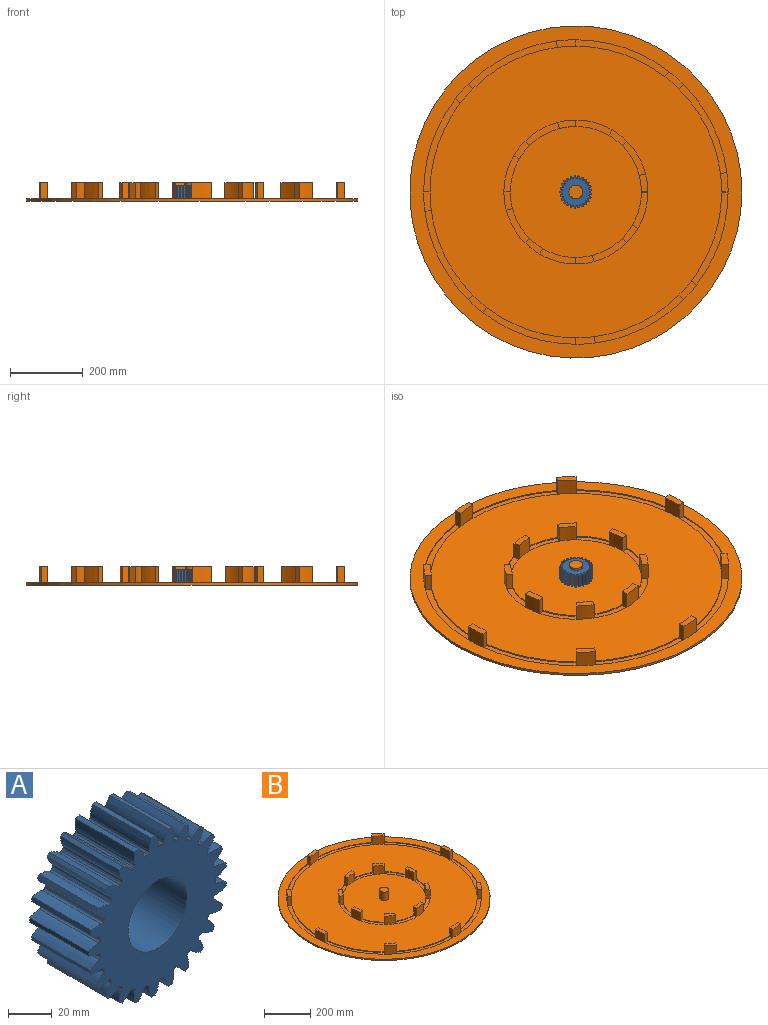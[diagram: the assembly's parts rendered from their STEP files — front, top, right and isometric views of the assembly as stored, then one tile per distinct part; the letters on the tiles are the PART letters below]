
ASSEMBLY  parts=2 mates=1
PART A: 153 faces, bbox 88.9x38.1x89.1 mm
  f0: cylinder r=44.58mm len=38.1mm, axis (0,1,0), area 90.4mm2, adj f24,f26,f137,f149
  f1: cylinder r=44.58mm len=38.1mm, axis (0,1,0), area 90.4mm2, adj f24,f26,f144,f147
  f2: cylinder r=44.58mm len=38.1mm, axis (0,1,0), area 90.4mm2, adj f24,f26,f132,f139
  f3: cylinder r=44.58mm len=38.1mm, axis (0,1,0), area 90.4mm2, adj f24,f26,f127,f134
  f4: cylinder r=44.58mm len=38.1mm, axis (0,1,0), area 90.4mm2, adj f24,f26,f122,f129
  f5: cylinder r=44.58mm len=38.1mm, axis (0,1,0), area 90.4mm2, adj f24,f26,f112,f124
  f6: cylinder r=44.58mm len=38.1mm, axis (0,1,0), area 90.4mm2, adj f24,f26,f107,f119
  f7: cylinder r=44.58mm len=38.1mm, axis (0,1,0), area 90.4mm2, adj f24,f26,f114,f117
  f8: cylinder r=44.58mm len=38.1mm, axis (0,1,0), area 90.4mm2, adj f24,f26,f102,f109
  f9: cylinder r=44.58mm len=38.1mm, axis (0,1,0), area 90.4mm2, adj f24,f26,f97,f104
  f10: cylinder r=44.58mm len=38.1mm, axis (0,1,0), area 90.4mm2, adj f24,f26,f92,f99
  f11: cylinder r=44.58mm len=38.1mm, axis (0,1,0), area 90.4mm2, adj f24,f26,f77,f94
  f12: cylinder r=44.58mm len=38.1mm, axis (0,1,0), area 90.4mm2, adj f24,f26,f27,f89
  f13: cylinder r=44.58mm len=38.1mm, axis (0,1,0), area 90.4mm2, adj f24,f26,f84,f87
  f14: cylinder r=44.58mm len=38.1mm, axis (0,1,0), area 90.4mm2, adj f24,f26,f72,f79
  f15: cylinder r=44.58mm len=38.1mm, axis (0,1,0), area 90.4mm2, adj f24,f26,f74,f82
  f16: cylinder r=44.58mm len=38.1mm, axis (0,1,0), area 90.4mm2, adj f24,f26,f69,f142
  f17: cylinder r=44.58mm len=38.1mm, axis (0,1,0), area 90.4mm2, adj f24,f26,f64,f67
  f18: cylinder r=44.58mm len=38.1mm, axis (0,1,0), area 90.4mm2, adj f24,f26,f59,f62
  f19: cylinder r=44.58mm len=38.1mm, axis (0,1,0), area 90.4mm2, adj f24,f26,f54,f57
  f20: cylinder r=44.58mm len=38.1mm, axis (0,1,0), area 90.4mm2, adj f24,f26,f42,f49
  f21: cylinder r=44.58mm len=38.1mm, axis (0,1,0), area 90.4mm2, adj f24,f26,f32,f44
  f22: cylinder r=44.58mm len=38.1mm, axis (0,1,0), area 90.4mm2, adj f24,f26,f39,f52
  f23: cylinder r=44.58mm len=38.1mm, axis (0,1,0), area 90.4mm2, adj f24,f26,f34,f37
  f24: plane 89.11x88.94mm, normal (0,-1,0), area 4133mm2, adj f0,f1,f2,f3,f4,f5,f6,f7
  f25: cylinder r=44.58mm len=38.1mm, axis (0,1,0), area 90.4mm2, adj f24,f26,f29,f47
  f26: plane 89.11x88.94mm, normal (0,1,0), area 4133mm2, adj f0,f1,f2,f3,f4,f5,f6,f7
  f27: extruded ~38.1x6.03mm, area 252.8mm2, adj f12,f24,f26,f30
  f28: cylinder r=37.15mm len=38.1mm, axis (0,1,0), area 43.2mm2, adj f24,f26,f30,f31
  f29: extruded ~38.1x6.03mm, area 252.8mm2, adj f24,f25,f26,f31
  f30: cylinder r=1.25mm len=38.1mm, axis (0,1,0), area 73.2mm2, adj f24,f26,f27,f28
  f31: cylinder r=1.25mm len=38.1mm, axis (0,1,0), area 73.2mm2, adj f24,f26,f28,f29
  f32: extruded ~38.1x6.16mm, area 252.8mm2, adj f21,f24,f26,f35
  f33: cylinder r=37.15mm len=38.1mm, axis (0,1,0), area 43.2mm2, adj f24,f26,f35,f36
  f34: extruded ~38.1x6mm, area 252.8mm2, adj f23,f24,f26,f36
  f35: cylinder r=1.25mm len=38.1mm, axis (0,1,0), area 73.2mm2, adj f24,f26,f32,f33
  f36: cylinder r=1.25mm len=38.1mm, axis (0,1,0), area 73.2mm2, adj f24,f26,f33,f34
  f37: extruded ~38.1x5.4mm, area 252.8mm2, adj f23,f24,f26,f40
  f38: cylinder r=37.15mm len=38.1mm, axis (0,1,0), area 43.2mm2, adj f24,f26,f40,f41
  f39: extruded ~38.1x6.47mm, area 252.8mm2, adj f22,f24,f26,f41
  f40: cylinder r=1.25mm len=38.1mm, axis (0,1,0), area 73.2mm2, adj f24,f26,f37,f38
  f41: cylinder r=1.25mm len=38.1mm, axis (0,1,0), area 73.2mm2, adj f24,f26,f38,f39
  f42: extruded ~38.1x6.52mm, area 252.8mm2, adj f20,f24,f26,f45
  f43: cylinder r=37.15mm len=38.1mm, axis (0,1,0), area 43.2mm2, adj f24,f26,f45,f46
  f44: extruded ~38.1x5.16mm, area 252.8mm2, adj f21,f24,f26,f46
  f45: cylinder r=1.25mm len=38.1mm, axis (0,1,0), area 73.2mm2, adj f24,f26,f42,f43
  f46: cylinder r=1.25mm len=38.1mm, axis (0,1,0), area 73.2mm2, adj f24,f26,f43,f44
  f47: extruded ~38.1x6.48mm, area 252.8mm2, adj f24,f25,f26,f50
  f48: cylinder r=37.15mm len=38.1mm, axis (0,1,0), area 43.2mm2, adj f24,f26,f50,f51
  f49: extruded ~38.1x5.2mm, area 252.8mm2, adj f20,f24,f26,f51
  f50: cylinder r=1.25mm len=38.1mm, axis (0,1,0), area 73.2mm2, adj f24,f26,f47,f48
  f51: cylinder r=1.25mm len=38.1mm, axis (0,1,0), area 73.2mm2, adj f24,f26,f48,f49
  f52: extruded ~38.1x4.94mm, area 252.8mm2, adj f22,f24,f26,f55
  f53: cylinder r=37.15mm len=38.1mm, axis (0,1,0), area 43.2mm2, adj f24,f26,f55,f56
  f54: extruded ~38.1x6.53mm, area 252.8mm2, adj f19,f24,f26,f56
  f55: cylinder r=1.25mm len=38.1mm, axis (0,1,0), area 73.2mm2, adj f24,f26,f52,f53
  f56: cylinder r=1.25mm len=38.1mm, axis (0,1,0), area 73.2mm2, adj f24,f26,f53,f54
  f57: extruded ~38.1x5.85mm, area 252.8mm2, adj f19,f24,f26,f60
  f58: cylinder r=37.15mm len=38.1mm, axis (0,1,0), area 43.2mm2, adj f24,f26,f60,f61
  f59: extruded ~38.1x6.18mm, area 252.8mm2, adj f18,f24,f26,f61
  f60: cylinder r=1.25mm len=38.1mm, axis (0,1,0), area 73.2mm2, adj f24,f26,f57,f58
  f61: cylinder r=1.25mm len=38.1mm, axis (0,1,0), area 73.2mm2, adj f24,f26,f58,f59
  f62: extruded ~38.1x6.4mm, area 252.8mm2, adj f18,f24,f26,f65
  f63: cylinder r=37.15mm len=38.1mm, axis (0,1,0), area 43.2mm2, adj f24,f26,f65,f66
  f64: extruded ~38.1x5.44mm, area 252.8mm2, adj f17,f24,f26,f66
  f65: cylinder r=1.25mm len=38.1mm, axis (0,1,0), area 73.2mm2, adj f24,f26,f62,f63
  f66: cylinder r=1.25mm len=38.1mm, axis (0,1,0), area 73.2mm2, adj f24,f26,f63,f64
  f67: extruded ~38.1x6.55mm, area 252.8mm2, adj f17,f24,f26,f70
  f68: cylinder r=37.15mm len=38.1mm, axis (0,1,0), area 43.2mm2, adj f24,f26,f70,f71
  f69: extruded ~38.1x4.89mm, area 252.8mm2, adj f16,f24,f26,f71
  f70: cylinder r=1.25mm len=38.1mm, axis (0,1,0), area 73.2mm2, adj f24,f26,f67,f68
  f71: cylinder r=1.25mm len=38.1mm, axis (0,1,0), area 73.2mm2, adj f24,f26,f68,f69
  f72: extruded ~38.1x6mm, area 252.8mm2, adj f14,f24,f26,f75
  f73: cylinder r=37.15mm len=38.1mm, axis (0,1,0), area 43.2mm2, adj f24,f26,f75,f76
  f74: extruded ~38.1x6.16mm, area 252.8mm2, adj f15,f24,f26,f76
  f75: cylinder r=1.25mm len=38.1mm, axis (0,1,0), area 73.2mm2, adj f24,f26,f72,f73
  f76: cylinder r=1.25mm len=38.1mm, axis (0,1,0), area 73.2mm2, adj f24,f26,f73,f74
  f77: extruded ~38.1x6.47mm, area 252.8mm2, adj f11,f24,f26,f80
  f78: cylinder r=37.15mm len=38.1mm, axis (0,1,0), area 43.2mm2, adj f24,f26,f80,f81
  f79: extruded ~38.1x5.4mm, area 252.8mm2, adj f14,f24,f26,f81
  f80: cylinder r=1.25mm len=38.1mm, axis (0,1,0), area 73.2mm2, adj f24,f26,f77,f78
  f81: cylinder r=1.25mm len=38.1mm, axis (0,1,0), area 73.2mm2, adj f24,f26,f78,f79
  f82: extruded ~38.1x5.16mm, area 252.8mm2, adj f15,f24,f26,f85
  f83: cylinder r=37.15mm len=38.1mm, axis (0,1,0), area 43.2mm2, adj f24,f26,f85,f86
  f84: extruded ~38.1x6.52mm, area 252.8mm2, adj f13,f24,f26,f86
  f85: cylinder r=1.25mm len=38.1mm, axis (0,1,0), area 73.2mm2, adj f24,f26,f82,f83
  f86: cylinder r=1.25mm len=38.1mm, axis (0,1,0), area 73.2mm2, adj f24,f26,f83,f84
  f87: extruded ~38.1x5.2mm, area 252.8mm2, adj f13,f24,f26,f90
  f88: cylinder r=37.15mm len=38.1mm, axis (0,1,0), area 43.2mm2, adj f24,f26,f90,f91
  f89: extruded ~38.1x6.48mm, area 252.8mm2, adj f12,f24,f26,f91
  f90: cylinder r=1.25mm len=38.1mm, axis (0,1,0), area 73.2mm2, adj f24,f26,f87,f88
  f91: cylinder r=1.25mm len=38.1mm, axis (0,1,0), area 73.2mm2, adj f24,f26,f88,f89
  f92: extruded ~38.1x6.53mm, area 252.8mm2, adj f10,f24,f26,f95
  f93: cylinder r=37.15mm len=38.1mm, axis (0,1,0), area 43.2mm2, adj f24,f26,f95,f96
  f94: extruded ~38.1x4.94mm, area 252.8mm2, adj f11,f24,f26,f96
  f95: cylinder r=1.25mm len=38.1mm, axis (0,1,0), area 73.2mm2, adj f24,f26,f92,f93
  f96: cylinder r=1.25mm len=38.1mm, axis (0,1,0), area 73.2mm2, adj f24,f26,f93,f94
  f97: extruded ~38.1x6.18mm, area 252.8mm2, adj f9,f24,f26,f100
  f98: cylinder r=37.15mm len=38.1mm, axis (0,1,0), area 43.2mm2, adj f24,f26,f100,f101
  f99: extruded ~38.1x5.85mm, area 252.8mm2, adj f10,f24,f26,f101
  f100: cylinder r=1.25mm len=38.1mm, axis (0,1,0), area 73.2mm2, adj f24,f26,f97,f98
  f101: cylinder r=1.25mm len=38.1mm, axis (0,1,0), area 73.2mm2, adj f24,f26,f98,f99
  f102: extruded ~38.1x5.44mm, area 252.8mm2, adj f8,f24,f26,f105
  f103: cylinder r=37.15mm len=38.1mm, axis (0,1,0), area 43.2mm2, adj f24,f26,f105,f106
  f104: extruded ~38.1x6.4mm, area 252.8mm2, adj f9,f24,f26,f106
  f105: cylinder r=1.25mm len=38.1mm, axis (0,1,0), area 73.2mm2, adj f24,f26,f102,f103
  f106: cylinder r=1.25mm len=38.1mm, axis (0,1,0), area 73.2mm2, adj f24,f26,f103,f104
  f107: extruded ~38.1x4.89mm, area 252.8mm2, adj f6,f24,f26,f110
  f108: cylinder r=37.15mm len=38.1mm, axis (0,1,0), area 43.2mm2, adj f24,f26,f110,f111
  f109: extruded ~38.1x6.55mm, area 252.8mm2, adj f8,f24,f26,f111
  f110: cylinder r=1.25mm len=38.1mm, axis (0,1,0), area 73.2mm2, adj f24,f26,f107,f108
  f111: cylinder r=1.25mm len=38.1mm, axis (0,1,0), area 73.2mm2, adj f24,f26,f108,f109
  f112: extruded ~38.1x6.39mm, area 252.8mm2, adj f5,f24,f26,f115
  f113: cylinder r=37.15mm len=38.1mm, axis (0,1,0), area 43.2mm2, adj f24,f26,f115,f116
  f114: extruded ~38.1x5.62mm, area 252.8mm2, adj f7,f24,f26,f116
  f115: cylinder r=1.25mm len=38.1mm, axis (0,1,0), area 73.2mm2, adj f24,f26,f112,f113
  f116: cylinder r=1.25mm len=38.1mm, axis (0,1,0), area 73.2mm2, adj f24,f26,f113,f114
  f117: extruded ~38.1x5.82mm, area 252.8mm2, adj f7,f24,f26,f120
  f118: cylinder r=37.15mm len=38.1mm, axis (0,1,0), area 43.2mm2, adj f24,f26,f120,f121
  f119: extruded ~38.1x6.28mm, area 252.8mm2, adj f6,f24,f26,f121
  f120: cylinder r=1.25mm len=38.1mm, axis (0,1,0), area 73.2mm2, adj f24,f26,f117,f118
  f121: cylinder r=1.25mm len=38.1mm, axis (0,1,0), area 73.2mm2, adj f24,f26,f118,f119
  f122: extruded ~38.1x6.55mm, area 252.8mm2, adj f4,f24,f26,f125
  f123: cylinder r=37.15mm len=38.1mm, axis (0,1,0), area 43.2mm2, adj f24,f26,f125,f126
  f124: extruded ~38.1x4.66mm, area 252.8mm2, adj f5,f24,f26,f126
  f125: cylinder r=1.25mm len=38.1mm, axis (0,1,0), area 73.2mm2, adj f24,f26,f122,f123
  f126: cylinder r=1.25mm len=38.1mm, axis (0,1,0), area 73.2mm2, adj f24,f26,f123,f124
  f127: extruded ~38.1x6.3mm, area 252.8mm2, adj f3,f24,f26,f130
  f128: cylinder r=37.15mm len=38.1mm, axis (0,1,0), area 43.2mm2, adj f24,f26,f130,f131
  f129: extruded ~38.1x5.66mm, area 252.8mm2, adj f4,f24,f26,f131
  f130: cylinder r=1.25mm len=38.1mm, axis (0,1,0), area 73.2mm2, adj f24,f26,f127,f128
  f131: cylinder r=1.25mm len=38.1mm, axis (0,1,0), area 73.2mm2, adj f24,f26,f128,f129
  f132: extruded ~38.1x5.66mm, area 252.8mm2, adj f2,f24,f26,f135
  f133: cylinder r=37.15mm len=38.1mm, axis (0,1,0), area 43.2mm2, adj f24,f26,f135,f136
  f134: extruded ~38.1x6.3mm, area 252.8mm2, adj f3,f24,f26,f136
  f135: cylinder r=1.25mm len=38.1mm, axis (0,1,0), area 73.2mm2, adj f24,f26,f132,f133
  f136: cylinder r=1.25mm len=38.1mm, axis (0,1,0), area 73.2mm2, adj f24,f26,f133,f134
  f137: extruded ~38.1x4.66mm, area 252.8mm2, adj f0,f24,f26,f140
  f138: cylinder r=37.15mm len=38.1mm, axis (0,1,0), area 43.2mm2, adj f24,f26,f140,f141
  f139: extruded ~38.1x6.55mm, area 252.8mm2, adj f2,f24,f26,f141
  f140: cylinder r=1.25mm len=38.1mm, axis (0,1,0), area 73.2mm2, adj f24,f26,f137,f138
  f141: cylinder r=1.25mm len=38.1mm, axis (0,1,0), area 73.2mm2, adj f24,f26,f138,f139
  f142: extruded ~38.1x6.28mm, area 252.8mm2, adj f16,f24,f26,f145
  f143: cylinder r=37.15mm len=38.1mm, axis (0,1,0), area 43.2mm2, adj f24,f26,f145,f146
  f144: extruded ~38.1x5.82mm, area 252.8mm2, adj f1,f24,f26,f146
  f145: cylinder r=1.25mm len=38.1mm, axis (0,1,0), area 73.2mm2, adj f24,f26,f142,f143
  f146: cylinder r=1.25mm len=38.1mm, axis (0,1,0), area 73.2mm2, adj f24,f26,f143,f144
  f147: extruded ~38.1x5.62mm, area 252.8mm2, adj f1,f24,f26,f150
  f148: cylinder r=37.15mm len=38.1mm, axis (0,1,0), area 43.2mm2, adj f24,f26,f150,f151
  f149: extruded ~38.1x6.39mm, area 252.8mm2, adj f0,f24,f26,f151
  f150: cylinder r=1.25mm len=38.1mm, axis (0,1,0), area 73.2mm2, adj f24,f26,f147,f148
  f151: cylinder r=1.25mm len=38.1mm, axis (0,1,0), area 73.2mm2, adj f24,f26,f148,f149
  f152: cylinder r=19.05mm len=38.1mm, axis (0,1,0), area 4560.4mm2, adj f24,f26
PART B: 135 faces, bbox 914.4x914.4x50.8 mm
  f0: cylinder r=180.34mm len=81.98mm, axis (0,0,-1), area 303.5mm2, adj f5,f52,f125,f130
  f1: cylinder r=198.12mm len=90.07mm, axis (0,0,-1), area 333.5mm2, adj f5,f51,f125,f130
  f2: plane 100.18x42.53mm, normal (0,0,1), area 1783.7mm2, adj f21,f50,f95,f131
  f3: cylinder r=180.34mm len=91.19mm, axis (0,0,-1), area 303.5mm2, adj f8,f52,f120,f126
  f4: cylinder r=198.12mm len=100.18mm, axis (0,0,-1), area 333.5mm2, adj f8,f51,f120,f126
  f5: plane 94.56x64.18mm, normal (0,0,1), area 1783.7mm2, adj f0,f1,f125,f130
  f6: cylinder r=180.34mm len=81.98mm, axis (0,0,-1), area 303.5mm2, adj f17,f52,f116,f121
  f7: cylinder r=198.12mm len=90.07mm, axis (0,0,-1), area 333.5mm2, adj f17,f51,f116,f121
  f8: plane 100.18x42.53mm, normal (0,0,1), area 1783.7mm2, adj f3,f4,f120,f126
  f9: cylinder r=180.34mm len=91.19mm, axis (0,0,-1), area 303.5mm2, adj f11,f52,f111,f115
  f10: cylinder r=198.12mm len=100.18mm, axis (0,0,-1), area 333.5mm2, adj f11,f51,f111,f115
  f11: plane 100.18x42.53mm, normal (0,0,1), area 1783.7mm2, adj f9,f10,f111,f115
  f12: cylinder r=180.34mm len=81.98mm, axis (0,0,-1), area 303.5mm2, adj f14,f52,f105,f110
  f13: cylinder r=198.12mm len=90.07mm, axis (0,0,-1), area 333.5mm2, adj f14,f51,f105,f110
  f14: plane 94.56x64.18mm, normal (0,0,1), area 1783.7mm2, adj f12,f13,f105,f110
  f15: cylinder r=180.34mm len=91.19mm, axis (0,0,-1), area 303.5mm2, adj f22,f52,f101,f106
  f16: cylinder r=198.12mm len=100.18mm, axis (0,0,-1), area 333.5mm2, adj f22,f51,f101,f106
  f17: plane 94.56x64.18mm, normal (0,0,1), area 1783.7mm2, adj f6,f7,f116,f121
  f18: cylinder r=180.34mm len=81.98mm, axis (0,0,-1), area 303.5mm2, adj f20,f52,f96,f100
  f19: cylinder r=198.12mm len=90.07mm, axis (0,0,-1), area 333.5mm2, adj f20,f51,f96,f100
  f20: plane 94.56x64.18mm, normal (0,0,1), area 1783.7mm2, adj f18,f19,f96,f100
  f21: cylinder r=180.34mm len=91.19mm, axis (0,0,-1), area 303.5mm2, adj f2,f52,f95,f131
  f22: plane 100.18x42.53mm, normal (0,0,1), area 1783.7mm2, adj f15,f16,f101,f106
  f23: cylinder r=401.32mm len=232.7mm, axis (0,0,-1), area 838.1mm2, adj f25,f51,f86,f90
  f24: cylinder r=419.1mm len=243mm, axis (0,0,-1), area 875.3mm2, adj f25,f49,f86,f90
  f25: plane 245.27x131.92mm, normal (0,0,1), area 4797.5mm2, adj f23,f24,f86,f90
  f26: cylinder r=401.32mm len=245.35mm, axis (0,0,-1), area 838.1mm2, adj f43,f51,f81,f85
  f27: cylinder r=419.1mm len=256.22mm, axis (0,0,-1), area 875.3mm2, adj f43,f49,f81,f85
  f28: plane 256.22x101.51mm, normal (0,0,1), area 4797.5mm2, adj f44,f48,f55,f91
  f29: cylinder r=401.32mm len=232.7mm, axis (0,0,-1), area 838.1mm2, adj f31,f51,f76,f80
  f30: cylinder r=419.1mm len=243mm, axis (0,0,-1), area 875.3mm2, adj f31,f49,f76,f80
  f31: plane 245.27x131.92mm, normal (0,0,1), area 4797.5mm2, adj f29,f30,f76,f80
  f32: cylinder r=401.32mm len=245.35mm, axis (0,0,-1), area 838.1mm2, adj f34,f51,f71,f75
  f33: cylinder r=419.1mm len=256.22mm, axis (0,0,-1), area 875.3mm2, adj f34,f49,f71,f75
  f34: plane 256.22x101.51mm, normal (0,0,1), area 4797.5mm2, adj f32,f33,f71,f75
  f35: cylinder r=401.32mm len=232.7mm, axis (0,0,-1), area 838.1mm2, adj f37,f51,f66,f70
  f36: cylinder r=419.1mm len=243mm, axis (0,0,-1), area 875.3mm2, adj f37,f49,f66,f70
  f37: plane 245.27x131.92mm, normal (0,0,1), area 4797.5mm2, adj f35,f36,f66,f70
  f38: cylinder r=401.32mm len=245.35mm, axis (0,0,-1), area 838.1mm2, adj f40,f51,f60,f65
  f39: cylinder r=419.1mm len=256.22mm, axis (0,0,-1), area 875.3mm2, adj f40,f49,f60,f65
  f40: plane 256.22x101.51mm, normal (0,0,1), area 4797.5mm2, adj f38,f39,f60,f65
  f41: cylinder r=401.32mm len=232.7mm, axis (0,0,-1), area 838.1mm2, adj f45,f51,f56,f61
  f42: cylinder r=419.1mm len=243mm, axis (0,0,-1), area 875.3mm2, adj f45,f49,f56,f61
  f43: plane 256.22x101.51mm, normal (0,0,1), area 4797.5mm2, adj f26,f27,f81,f85
  f44: cylinder r=401.32mm len=245.35mm, axis (0,0,-1), area 838.1mm2, adj f28,f51,f55,f91
  f45: plane 245.27x131.92mm, normal (0,0,1), area 4797.5mm2, adj f41,f42,f56,f61
  f46: cylinder r=457.2mm len=914.4mm, axis (0,0,-1), area 18241.5mm2, adj f47,f49
  f47: plane 914.4x914.4mm, normal (0,0,-1), area 656692.9mm2, adj f46
  f48: cylinder r=419.1mm len=256.22mm, axis (0,0,-1), area 875.3mm2, adj f28,f49,f55,f91
  f49: plane 914.4x914.4mm, normal (0,0,1), area 104888.4mm2, adj f24,f27,f30,f33,f36,f39,f42,f46
  f50: cylinder r=198.12mm len=100.18mm, axis (0,0,-1), area 333.5mm2, adj f2,f51,f95,f131
  f51: plane 802.64x802.64mm, normal (0,0,1), area 382665.5mm2, adj f1,f4,f7,f10,f13,f16,f19,f23
  f52: plane 360.68x360.68mm, normal (0,0,1), area 101032.4mm2, adj f0,f3,f6,f9,f12,f15,f18,f21
  f53: cylinder r=419.1mm len=53.34mm, axis (0,0,-1), area 2377.6mm2, adj f49,f55,f56,f57
  f54: cylinder r=401.32mm len=51.08mm, axis (0,0,-1), area 2276.7mm2, adj f51,f55,f56,f57
  f55: plane 47.63x17.78mm, normal (0,-1,0), area 846.8mm2, adj f28,f44,f48,f53,f54,f57
  f56: plane 47.63x17.64mm, normal (-0.13,0.99,0), area 846.8mm2, adj f41,f42,f45,f53,f54,f57
  f57: plane 53.34x21.04mm, normal (0,0,1), area 930.9mm2, adj f53,f54,f55,f56
  f58: cylinder r=419.1mm len=44.45mm, axis (0,0,-1), area 2377.6mm2, adj f49,f60,f61,f62
  f59: cylinder r=401.32mm len=44.45mm, axis (0,0,-1), area 2276.7mm2, adj f51,f60,f61,f62
  f60: plane 47.63x14.07mm, normal (-0.79,0.61,0), area 846.8mm2, adj f38,f39,f40,f58,f59,f62
  f61: plane 47.63x12.57mm, normal (0.71,-0.71,0), area 846.8mm2, adj f41,f42,f45,f58,f59,f62
  f62: plane 51x47.88mm, normal (0,0,1), area 930.9mm2, adj f58,f59,f60,f61
  f63: cylinder r=419.1mm len=53.34mm, axis (0,0,-1), area 2377.6mm2, adj f49,f65,f66,f67
  f64: cylinder r=401.32mm len=51.08mm, axis (0,0,-1), area 2276.7mm2, adj f51,f65,f66,f67
  f65: plane 47.63x17.78mm, normal (1,0,0), area 846.8mm2, adj f38,f39,f40,f63,f64,f67
  f66: plane 47.63x17.64mm, normal (-0.99,-0.13,0), area 846.8mm2, adj f35,f36,f37,f63,f64,f67
  f67: plane 53.34x21.04mm, normal (0,0,1), area 930.9mm2, adj f63,f64,f65,f66
  f68: cylinder r=419.1mm len=44.45mm, axis (0,0,-1), area 2377.6mm2, adj f49,f70,f71,f72
  f69: cylinder r=401.32mm len=44.45mm, axis (0,0,-1), area 2276.7mm2, adj f51,f70,f71,f72
  f70: plane 47.63x12.57mm, normal (0.71,0.71,0), area 846.8mm2, adj f35,f36,f37,f68,f69,f72
  f71: plane 47.63x14.07mm, normal (-0.61,-0.79,0), area 846.8mm2, adj f32,f33,f34,f68,f69,f72
  f72: plane 51x47.88mm, normal (0,0,1), area 930.9mm2, adj f68,f69,f70,f71
  f73: cylinder r=419.1mm len=53.34mm, axis (0,0,-1), area 2377.6mm2, adj f49,f75,f76,f77
  f74: cylinder r=401.32mm len=51.08mm, axis (0,0,-1), area 2276.7mm2, adj f51,f75,f76,f77
  f75: plane 47.63x17.78mm, normal (0,1,0), area 846.8mm2, adj f32,f33,f34,f73,f74,f77
  f76: plane 47.63x17.64mm, normal (0.13,-0.99,0), area 846.8mm2, adj f29,f30,f31,f73,f74,f77
  f77: plane 53.34x21.04mm, normal (0,0,1), area 930.9mm2, adj f73,f74,f75,f76
  f78: cylinder r=419.1mm len=44.45mm, axis (0,0,-1), area 2377.6mm2, adj f49,f80,f81,f82
  f79: cylinder r=401.32mm len=44.45mm, axis (0,0,-1), area 2276.7mm2, adj f51,f80,f81,f82
  f80: plane 47.63x12.57mm, normal (-0.71,0.71,0), area 846.8mm2, adj f29,f30,f31,f78,f79,f82
  f81: plane 47.63x14.07mm, normal (0.79,-0.61,0), area 846.8mm2, adj f26,f27,f43,f78,f79,f82
  f82: plane 51x47.88mm, normal (0,0,1), area 930.9mm2, adj f78,f79,f80,f81
  f83: cylinder r=419.1mm len=53.34mm, axis (0,0,-1), area 2377.6mm2, adj f49,f85,f86,f87
  f84: cylinder r=401.32mm len=51.08mm, axis (0,0,-1), area 2276.7mm2, adj f51,f85,f86,f87
  f85: plane 47.63x17.78mm, normal (-1,0,0), area 846.8mm2, adj f26,f27,f43,f83,f84,f87
  f86: plane 47.63x17.64mm, normal (0.99,0.13,0), area 846.8mm2, adj f23,f24,f25,f83,f84,f87
  f87: plane 53.34x21.04mm, normal (0,0,1), area 930.9mm2, adj f83,f84,f85,f86
  f88: cylinder r=419.1mm len=44.45mm, axis (0,0,-1), area 2377.6mm2, adj f49,f90,f91,f92
  f89: cylinder r=401.32mm len=44.45mm, axis (0,0,-1), area 2276.7mm2, adj f51,f90,f91,f92
  f90: plane 47.63x12.57mm, normal (-0.71,-0.71,0), area 846.8mm2, adj f23,f24,f25,f88,f89,f92
  f91: plane 47.63x14.07mm, normal (0.61,0.79,0), area 846.8mm2, adj f28,f44,f48,f88,f89,f92
  f92: plane 51x47.88mm, normal (0,0,1), area 930.9mm2, adj f88,f89,f90,f91
  f93: cylinder r=198.12mm len=50.02mm, axis (0,0,-1), area 2247.9mm2, adj f51,f95,f96,f97
  f94: cylinder r=180.34mm len=45.54mm, axis (0,0,-1), area 2046.2mm2, adj f52,f95,f96,f97
  f95: plane 47.63x17.78mm, normal (0,-1,0), area 846.8mm2, adj f2,f21,f50,f93,f94,f97
  f96: plane 47.63x17.2mm, normal (-0.25,0.97,0), area 846.8mm2, adj f18,f19,f20,f93,f94,f97
  f97: plane 50.02x23.62mm, normal (0,0,1), area 858.8mm2, adj f93,f94,f95,f96
  f98: cylinder r=198.12mm len=44.45mm, axis (0,0,-1), area 2247.9mm2, adj f51,f100,f101,f102
  f99: cylinder r=180.34mm len=44.45mm, axis (0,0,-1), area 2046.2mm2, adj f52,f100,f101,f102
  f100: plane 47.63x12.57mm, normal (0.71,-0.71,0), area 846.8mm2, adj f18,f19,f20,f98,f99,f102
  f101: plane 47.63x15.34mm, normal (-0.86,0.51,0), area 846.8mm2, adj f15,f16,f22,f98,f99,f102
  f102: plane 48.9x43.41mm, normal (0,0,1), area 858.8mm2, adj f98,f99,f100,f101
  f103: cylinder r=198.12mm len=50.02mm, axis (0,0,-1), area 2247.9mm2, adj f51,f105,f106,f107
  f104: cylinder r=180.34mm len=45.54mm, axis (0,0,-1), area 2046.2mm2, adj f52,f105,f106,f107
  f105: plane 47.63x17.2mm, normal (-0.97,-0.25,0), area 846.8mm2, adj f12,f13,f14,f103,f104,f107
  f106: plane 47.63x17.78mm, normal (1,0,0), area 846.8mm2, adj f15,f16,f22,f103,f104,f107
  f107: plane 50.02x23.62mm, normal (0,0,1), area 858.8mm2, adj f103,f104,f105,f106
  f108: cylinder r=198.12mm len=44.45mm, axis (0,0,-1), area 2247.9mm2, adj f51,f110,f111,f112
  f109: cylinder r=180.34mm len=44.45mm, axis (0,0,-1), area 2046.2mm2, adj f52,f110,f111,f112
  f110: plane 47.63x12.57mm, normal (0.71,0.71,0), area 846.8mm2, adj f12,f13,f14,f108,f109,f112
  f111: plane 47.63x15.34mm, normal (-0.51,-0.86,0), area 846.8mm2, adj f9,f10,f11,f108,f109,f112
  f112: plane 48.9x43.41mm, normal (0,0,1), area 858.8mm2, adj f108,f109,f110,f111
  f113: cylinder r=198.12mm len=50.02mm, axis (0,0,-1), area 2247.9mm2, adj f51,f115,f116,f117
  f114: cylinder r=180.34mm len=45.54mm, axis (0,0,-1), area 2046.2mm2, adj f52,f115,f116,f117
  f115: plane 47.63x17.78mm, normal (0,1,0), area 846.8mm2, adj f9,f10,f11,f113,f114,f117
  f116: plane 47.63x17.2mm, normal (0.25,-0.97,0), area 846.8mm2, adj f6,f7,f17,f113,f114,f117
  f117: plane 50.02x23.62mm, normal (0,0,1), area 858.8mm2, adj f113,f114,f115,f116
  f118: cylinder r=198.12mm len=44.45mm, axis (0,0,-1), area 2247.9mm2, adj f51,f120,f121,f122
  f119: cylinder r=180.34mm len=44.45mm, axis (0,0,-1), area 2046.2mm2, adj f52,f120,f121,f122
  f120: plane 47.63x15.34mm, normal (0.86,-0.51,0), area 846.8mm2, adj f3,f4,f8,f118,f119,f122
  f121: plane 47.63x12.57mm, normal (-0.71,0.71,0), area 846.8mm2, adj f6,f7,f17,f118,f119,f122
  f122: plane 48.9x43.41mm, normal (0,0,1), area 858.8mm2, adj f118,f119,f120,f121
  f123: cylinder r=198.12mm len=50.02mm, axis (0,0,-1), area 2247.9mm2, adj f51,f125,f126,f127
  f124: cylinder r=180.34mm len=45.54mm, axis (0,0,-1), area 2046.2mm2, adj f52,f125,f126,f127
  f125: plane 47.63x17.2mm, normal (0.97,0.25,0), area 846.8mm2, adj f0,f1,f5,f123,f124,f127
  f126: plane 47.63x17.78mm, normal (-1,0,0), area 846.8mm2, adj f3,f4,f8,f123,f124,f127
  f127: plane 50.02x23.62mm, normal (0,0,1), area 858.8mm2, adj f123,f124,f125,f126
  f128: cylinder r=198.12mm len=44.45mm, axis (0,0,-1), area 2247.9mm2, adj f51,f130,f131,f132
  f129: cylinder r=180.34mm len=44.45mm, axis (0,0,-1), area 2046.2mm2, adj f52,f130,f131,f132
  f130: plane 47.63x12.57mm, normal (-0.71,-0.71,0), area 846.8mm2, adj f0,f1,f5,f128,f129,f132
  f131: plane 47.63x15.34mm, normal (0.51,0.86,0), area 846.8mm2, adj f2,f21,f50,f128,f129,f132
  f132: plane 48.9x43.41mm, normal (0,0,1), area 858.8mm2, adj f128,f129,f130,f131
  f133: plane 38.1x38.1mm, normal (0,0,1), area 1140.1mm2, adj f134
  f134: cylinder r=19.05mm len=44.45mm, axis (0,0,-1), area 5320.4mm2, adj f52,f133
PLACE A rot(axis=(1,0,0),90deg) t=(0,0,44.45)mm
PLACE B at identity
MATE fastened A.f0 <-> B.f1  axis (0,0,-1) through (0,0,6.35)mm
